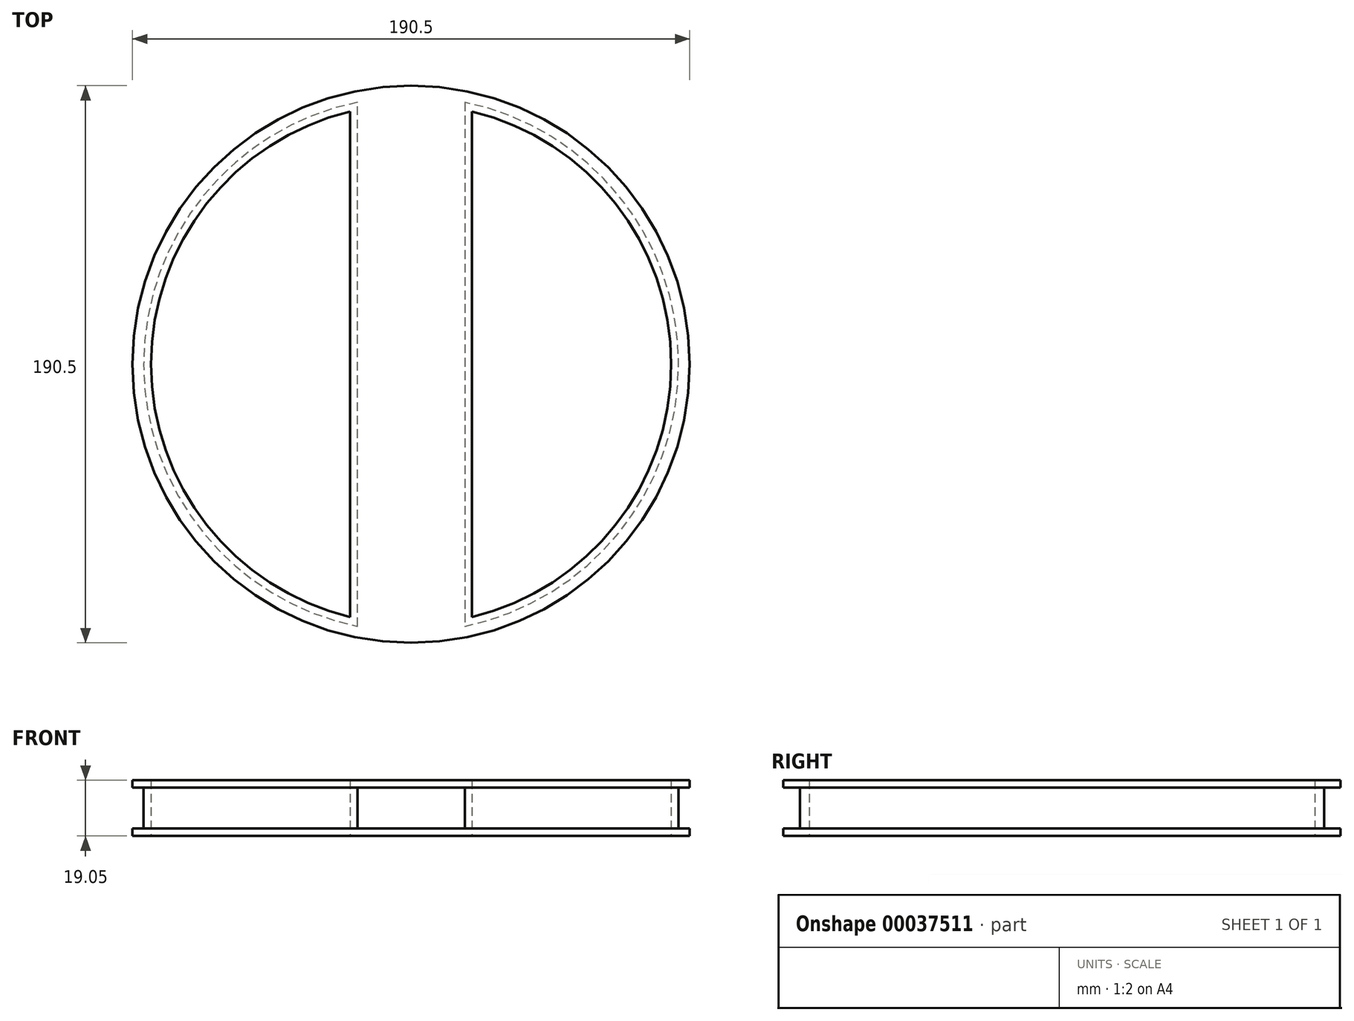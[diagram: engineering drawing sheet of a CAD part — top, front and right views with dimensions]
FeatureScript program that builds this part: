
annotation { "Feature Type Name" : "Feature", "Feature Type Description" : "" }
export const myFeature = defineFeature(function(context is Context, id is Id, definition is map)
    precondition{}
    {
        {
            var Q0;
            Q0=qCreatedBy(makeId("Top.planeOp"),FACE);
            var sketch = newSketch(context, id + "F0", { "sketchPlane" : qUnion([Q0])});
            skPoint(sketch, "E0", {"position": v(0, 88.9) * mm});
            skPoint(sketch, "E1", {"position": v(0, 95.25) * mm});
            skArc(sketch, "E2", {"start": v(-20.86, 86.42) * mm, "mid": v(-88.9, 0) * mm, "end": v(-20.86, -86.42) * mm});
            skCircle(sketch, "E3", {"center": v(0, 0) * mm, "radius": 95.25 * mm});
            skLineSegment(sketch, "E4", {"start": v(-20.86, 78.5) * mm, "end": v(-20.86, 86.42) * mm});
            skLineSegment(sketch, "E5", {"start": v(20.86, 86.42) * mm, "end": v(20.86, -86.42) * mm});
            skPoint(sketch, "E5.endSnap0", {"position": v(20.86, 78.5) * mm});
            skLineSegment(sketch, "E6", {"start": v(-20.86, -86.42) * mm, "end": v(-20.86, 78.5) * mm});
            skPoint(sketch, "E7.end.orphan", {"position": v(0, 78.5) * mm});
            skPoint(sketch, "E8.end.orphan", {"position": v(-41.73, 78.5) * mm});
            skPoint(sketch, "E9.end.orphan", {"position": v(41.73, 78.5) * mm});
            skArc(sketch, "E10.trimOffspring", {"start": v(20.86, -86.42) * mm, "mid": v(88.9, 0) * mm, "end": v(20.86, 86.42) * mm});
            skSolve(sketch);
        }
        {
            var Q0;
            Q0=makeQuery(id+"F0.imprint","IMPRINT",FACE,{"disambiguationData":[TD([[makeQuery(id+"F0.imprint","IMPRINT",EDGE,{"derivedFrom":sQuery(id+"F0.wireOp",EDGE,"E2")}),-1.0]])]});
            extrude(context, id + "F1", {"entities" : qUnion([Q0]), "depth" : 19.05 * mm});
        }
        {
            var Q0;
            Q0=makeQuery(id+"F1.opExtrude","SWEPT_FACE",FACE,{"disambiguationData":[OSD([sQuery(id+"F0.wireOp",EDGE,"E3")])]});
            shell(context, id + "F2", {"entities" : qUnion([Q0]), "thickness" : 2.54 * mm});
        }
    });
